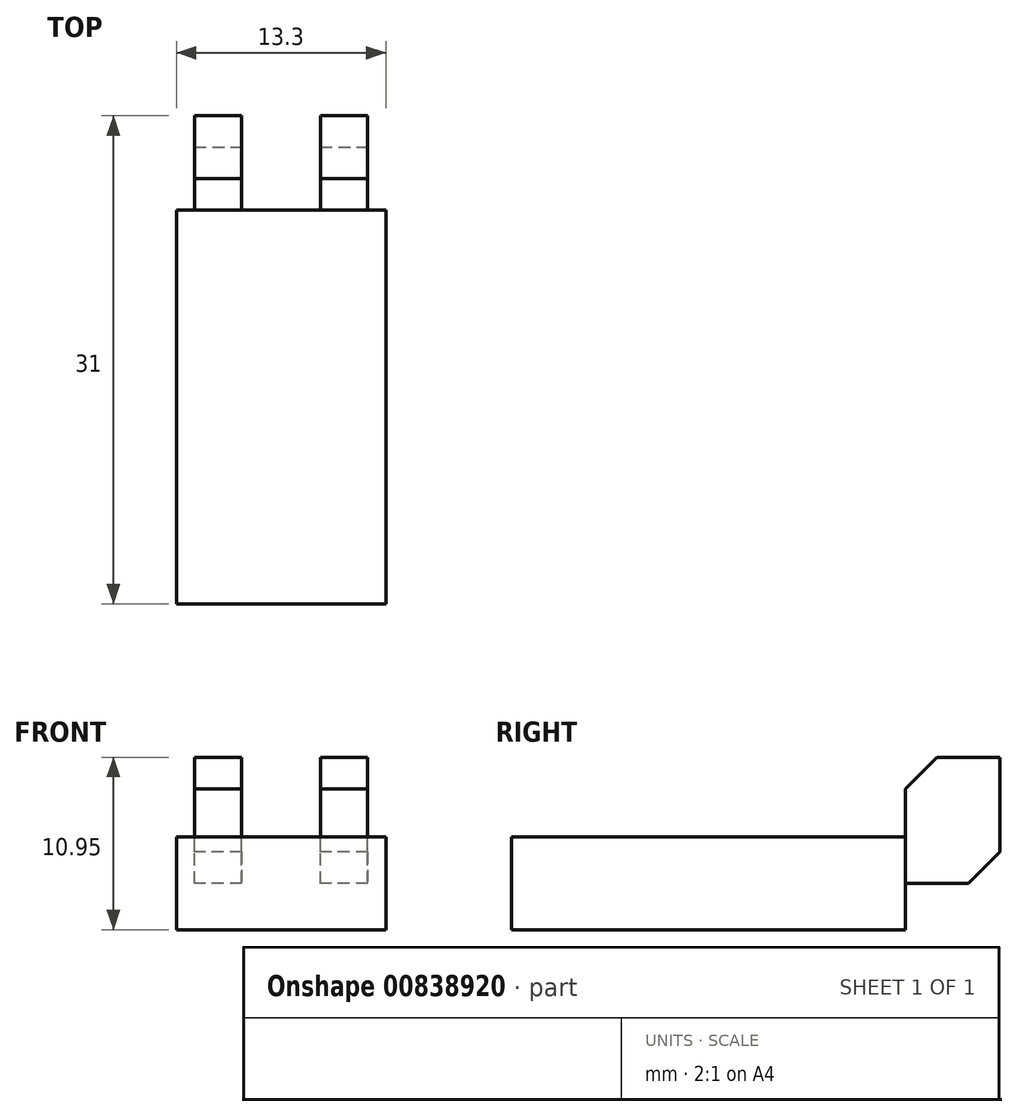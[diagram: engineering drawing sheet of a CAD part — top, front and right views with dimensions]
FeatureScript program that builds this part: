
annotation { "Feature Type Name" : "Feature", "Feature Type Description" : "" }
export const myFeature = defineFeature(function(context is Context, id is Id, definition is map)
    precondition{}
    {
        {
            var Q0;
            Q0=qCreatedBy(makeId("Front.planeOp"),FACE);
            var sketch = newSketch(context, id + "F0", { "sketchPlane" : qUnion([Q0])});
            skLineSegment(sketch, "E0.bottom", {"start": v(6.65, -2.95) * mm, "end": v(-6.65, -2.95) * mm});
            skLineSegment(sketch, "E0.top", {"start": v(6.65, 2.95) * mm, "end": v(-6.65, 2.95) * mm});
            skLineSegment(sketch, "E0.left", {"start": v(6.65, -2.95) * mm, "end": v(6.65, 2.95) * mm});
            skLineSegment(sketch, "E0.right", {"start": v(-6.65, -2.95) * mm, "end": v(-6.65, 2.95) * mm});
            skPoint(sketch, "E0.middle", {"position": v(0, 0) * mm});
            skSolve(sketch);
        }
        {
            var Q0;
            Q0 = qSketchRegion(id + "F0", true);
            extrude(context, id + "F1", {"entities" : qUnion([Q0]), "depth" : 25 * mm, "offsetDistance" : 25 * mm});
        }
        {
            var Q0;
            Q0=qCreatedBy(makeId("Front.planeOp"),FACE);
            var sketch = newSketch(context, id + "F2", { "sketchPlane" : qUnion([Q0])});
            skLineSegment(sketch, "E1.bottom", {"start": v(-2.5, 0) * mm, "end": v(-5.5, 0) * mm});
            skLineSegment(sketch, "E1.top", {"start": v(-2.5, 8) * mm, "end": v(-5.5, 8) * mm});
            skLineSegment(sketch, "E1.left", {"start": v(-2.5, 0) * mm, "end": v(-2.5, 8) * mm});
            skLineSegment(sketch, "E1.right", {"start": v(-5.5, 0) * mm, "end": v(-5.5, 8) * mm});
            skPoint(sketch, "E1.middle", {"position": v(-4, 4) * mm});
            skLineSegment(sketch, "E2.bottom", {"start": v(5.5, 0) * mm, "end": v(2.5, 0) * mm});
            skLineSegment(sketch, "E2.top", {"start": v(5.5, 8) * mm, "end": v(2.5, 8) * mm});
            skLineSegment(sketch, "E2.left", {"start": v(5.5, 0) * mm, "end": v(5.5, 8) * mm});
            skLineSegment(sketch, "E2.right", {"start": v(2.5, 0) * mm, "end": v(2.5, 8) * mm});
            skPoint(sketch, "E2.middle", {"position": v(4, 4) * mm});
            skSolve(sketch);
        }
        {
            var Q0;
            Q0 = qSketchRegion(id + "F2", true);
            extrude(context, id + "F3", {"entities" : qUnion([Q0]), "operationType" : NewBodyOperationType.ADD, "oppositeDirection" : true, "depth" : 6 * mm, "offsetDistance" : 25 * mm});
        }
        {
            var Q0;
            Q0=makeQuery(id+"F3.opExtrude","CAP_EDGE",EDGE,{"disambiguationData":[OSD([sQuery(id+"F2.wireOp",EDGE,"E1.top")])],"isStart":true});
            var Q1;
            Q1=makeQuery(id+"F3.opExtrude","CAP_EDGE",EDGE,{"disambiguationData":[OSD([sQuery(id+"F2.wireOp",EDGE,"E2.top")])],"isStart":true});
            var Q2;
            Q2=makeQuery(id+"F3.opExtrude","CAP_EDGE",EDGE,{"disambiguationData":[OSD([sQuery(id+"F2.wireOp",EDGE,"E2.bottom")])],"isStart":false});
            var Q3;
            Q3=makeQuery(id+"F3.opExtrude","CAP_EDGE",EDGE,{"disambiguationData":[OSD([sQuery(id+"F2.wireOp",EDGE,"E1.bottom")])],"isStart":false});
            chamfer(context, id + "F4", {"entities" : qUnion([Q0, Q1, Q2, Q3]), "width" : 2 * mm, "tangentPropagation" : true});
        }
    });
